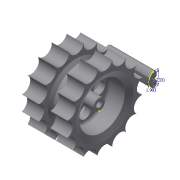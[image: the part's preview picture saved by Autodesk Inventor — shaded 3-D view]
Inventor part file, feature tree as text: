
AUTODESK INVENTOR PART (.ipt)
format: ipt  version: 2015 (Build 190159000, 159)  size: 294,912 bytes
history: native  units: mm
features: sketch x12, hole x4, revolve x1, extrude x1
ambient origin geometry x8: Origin, YZ Plane, XZ Plane, XY Plane, X Axis, Y Axis, Z Axis, Center Point
bodies: Solid1 (feature_tree)
feature tree (18):
  revolve  "Revolution1"  [1 undecoded]
  hole  "Hole1"  [1 undecoded]
  hole  "Hole2"  [1 undecoded]
  sketch  "Sketch4"  dims[d14=90.0deg d15=3.0mm]
  hole  "Hole3"  [1 undecoded]
  sketch  "Sketch6"  dims[d18=3.0mm]
  sketch  "Sketch7"  dims[d19=5.0mm d20=6.0mm d21=4.0mm d22=2.0mm d23=90.0deg d24=8.0mm d25=0.0mm d26=5.0mm]
  sketch  "Sketch8"  dims[d27=5.0mm]
  hole  "Hole4"  [1 undecoded]
  sketch  "Sketch9"  dims[d29=5.0mm]
  extrude  "Extrusion1"  Depth=5.0mm
  sketch  "Sketch11"  dims[d32=3.0mm]
  sketch  "Sketch12"  dims[d33=3.0mm d34=3.0mm d35=4.0mm d36=6.0mm d37=4.0mm d38=2.0mm d39=90.0deg d40=8.0mm d41=0.0mm d42=2.0mm d43=6.0mm d44=4.0mm d45=2.0mm d46=90.0deg d47=20.0mm d48=0.0mm d49=2.0mm d50=1.0mm d51=4.0mm d52=4.0mm d53=6.0mm d54=14.0mm d55=14.0mm d56=14.0mm d57=14.0mm d58=14.0mm d59=45.0deg d60=14.0mm d61=135.0deg d62=14.0mm d63=135.0deg d64=14.0mm d65=14.0mm d66=22.5deg d67=14.0mm d68=14.0mm d69=14.0mm d70=112.5deg d71=14.0mm d72=157.5deg d73=14.0mm d74=157.5deg d75=14.0mm d76=112.5deg d77=5.5mm d78=6.0mm d79=4.0mm d80=2.0mm d81=90.0deg d82=20.0mm d83=0.0mm d93=16.0mm d94=0.0mm d99=0.616266mm d102=1.902855mm d103=6.0mm d104=5.232531mm]
  sketch  "Sketch1"  dims[d0=6.0mm d1=2.0mm]
  sketch  "Sketch2"  dims[d3=5.0mm d6=12.0mm]
  sketch  "Sketch3"  dims[d7=2.0mm d8=5.0mm]
  sketch  "Sketch5"  dims[d16=3.0mm d17=3.0mm]
  sketch  "Sketch10"  dims[d31=3.0mm]
note: 5 required parameter values undecoded (feature->parameter linkage not recoverable at this tier; creation-order binding heuristic only, values carry confidence <= 0.55)